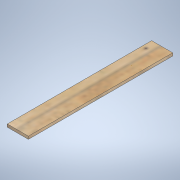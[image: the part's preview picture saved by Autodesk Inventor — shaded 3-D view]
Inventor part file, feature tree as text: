
AUTODESK INVENTOR PART (.ipt)
format: ipt  version: 2020 (Build 240168000, 168)  size: 182,272 bytes
history: native  units: mm
features: extrude x1, sketch x1
ambient origin geometry x8: Origin, YZ Plane, XZ Plane, XY Plane, X Axis, Y Axis, Z Axis, Center Point
bodies: Body1 (feature_tree)
feature tree (2):
  extrude  "Extrusion10"  Depth=4.0mm
  sketch  "Sketch9"  dims[d40=3.25mm d60=0.872665mm d61=12.566371mm d62=13.439035mm d171=30.0mm d172=205.29mm d173=4.0mm d174=0.0mm]
